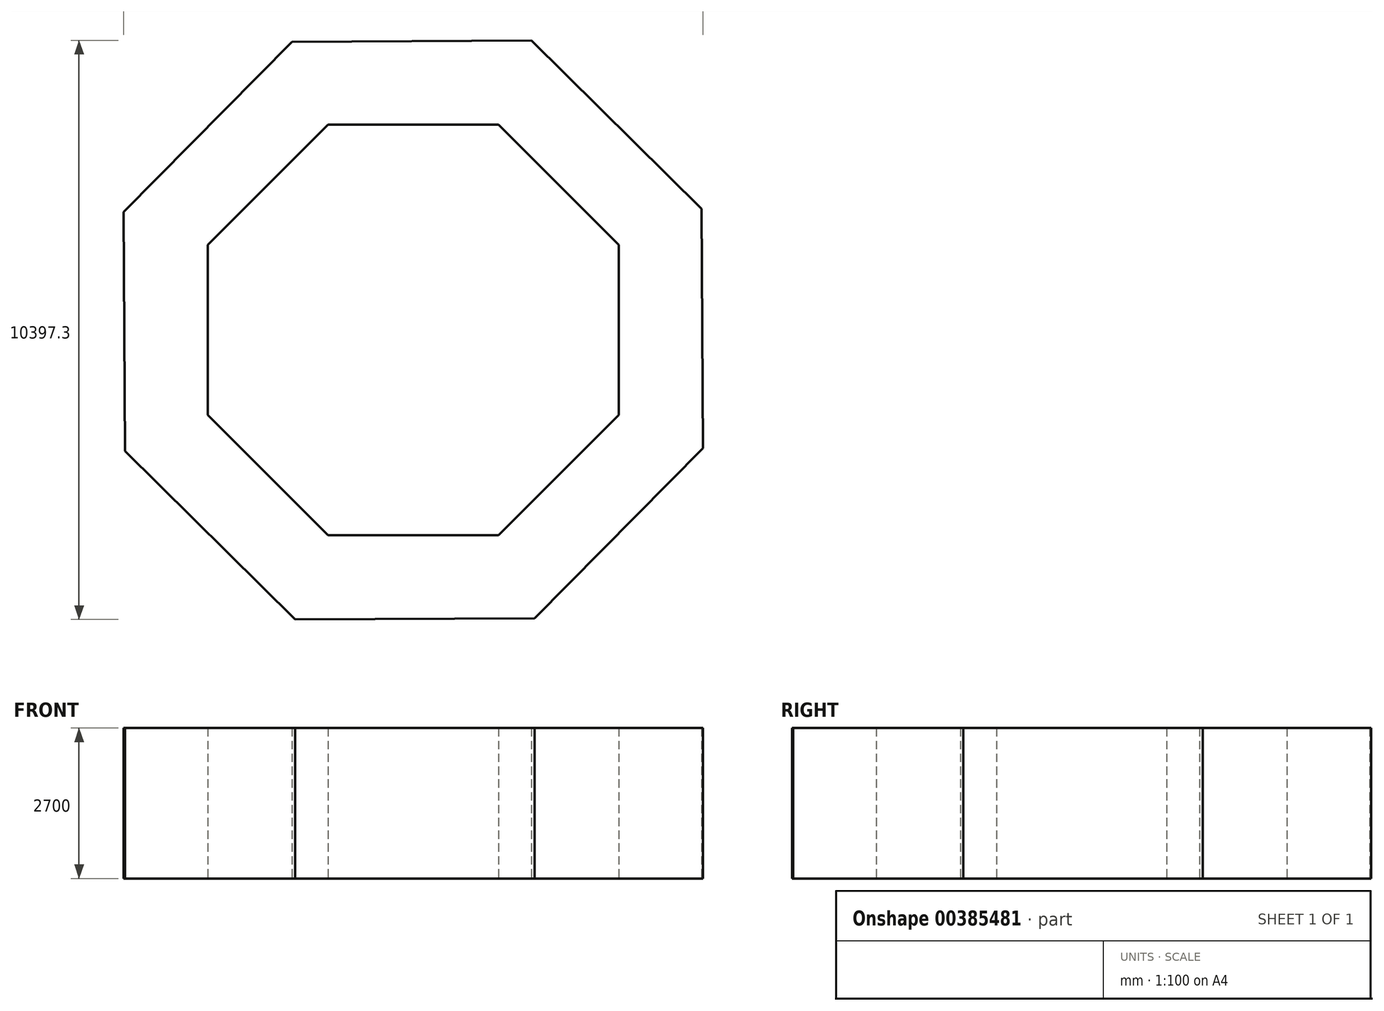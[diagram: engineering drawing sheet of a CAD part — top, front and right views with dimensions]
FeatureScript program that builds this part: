
annotation { "Feature Type Name" : "Feature", "Feature Type Description" : "" }
export const myFeature = defineFeature(function(context is Context, id is Id, definition is map)
    precondition{}
    {
        {
            var Q0;
            Q0=qCreatedBy(makeId("Top.planeOp"),FACE);
            var sketch = newSketch(context, id + "F0", { "sketchPlane" : qUnion([Q0])});
            skCircle(sketch, "E0.cCircle", {"center": v(0, 0) * mm, "radius": 5187 * mm, "construction": true});
            skLineSegment(sketch, "E0.0", {"start": v(-5175.2, -2176.78) * mm, "end": v(-5198.64, 2120.2) * mm});
            skLineSegment(sketch, "E0.1", {"start": v(-5198.64, 2120.2) * mm, "end": v(-2176.78, 5175.2) * mm});
            skLineSegment(sketch, "E0.2", {"start": v(-2176.78, 5175.2) * mm, "end": v(2120.2, 5198.64) * mm});
            skLineSegment(sketch, "E0.3", {"start": v(2120.2, 5198.64) * mm, "end": v(5175.2, 2176.78) * mm});
            skLineSegment(sketch, "E0.4", {"start": v(5175.2, 2176.78) * mm, "end": v(5198.64, -2120.2) * mm});
            skLineSegment(sketch, "E0.5", {"start": v(5198.64, -2120.2) * mm, "end": v(2176.78, -5175.2) * mm});
            skLineSegment(sketch, "E0.6", {"start": v(2176.78, -5175.2) * mm, "end": v(-2120.2, -5198.64) * mm});
            skLineSegment(sketch, "E0.7", {"start": v(-2120.2, -5198.64) * mm, "end": v(-5175.2, -2176.78) * mm});
            skPoint(sketch, "E0.0.midPoint", {"position": v(-5186.92, -28.29) * mm});
            skCircle(sketch, "E1.cCircle", {"center": v(0, 0) * mm, "radius": 3687.71 * mm, "construction": true});
            skPoint(sketch, "E1.cCircle.perimeterSnap0", {"position": v(-3647.7, -3687.71) * mm});
            skLineSegment(sketch, "E1.0", {"start": v(1527.5, -3687.71) * mm, "end": v(-1527.5, -3687.71) * mm});
            skLineSegment(sketch, "E1.1", {"start": v(-1527.5, -3687.71) * mm, "end": v(-3687.71, -1527.5) * mm});
            skLineSegment(sketch, "E1.2", {"start": v(-3687.71, -1527.5) * mm, "end": v(-3687.71, 1527.5) * mm});
            skLineSegment(sketch, "E1.3", {"start": v(-3687.71, 1527.5) * mm, "end": v(-1527.5, 3687.71) * mm});
            skLineSegment(sketch, "E1.4", {"start": v(-1527.5, 3687.71) * mm, "end": v(1527.5, 3687.71) * mm});
            skLineSegment(sketch, "E1.5", {"start": v(1527.5, 3687.71) * mm, "end": v(3687.71, 1527.5) * mm});
            skLineSegment(sketch, "E1.6", {"start": v(3687.71, 1527.5) * mm, "end": v(3687.71, -1527.5) * mm});
            skLineSegment(sketch, "E1.7", {"start": v(3687.71, -1527.5) * mm, "end": v(1527.5, -3687.71) * mm});
            skPoint(sketch, "E1.0.midPoint", {"position": v(0, -3687.71) * mm});
            skPoint(sketch, "E1.0.midPoint.positionSnap0", {"position": v(-3647.7, -3687.71) * mm});
            skSolve(sketch);
        }
        {
            var Q0;
            Q0=qSketchRegion(id+"F0",true);
            extrude(context, id + "F1", {"entities" : qUnion([Q0]), "depth" : 2700 * mm});
        }
    });
